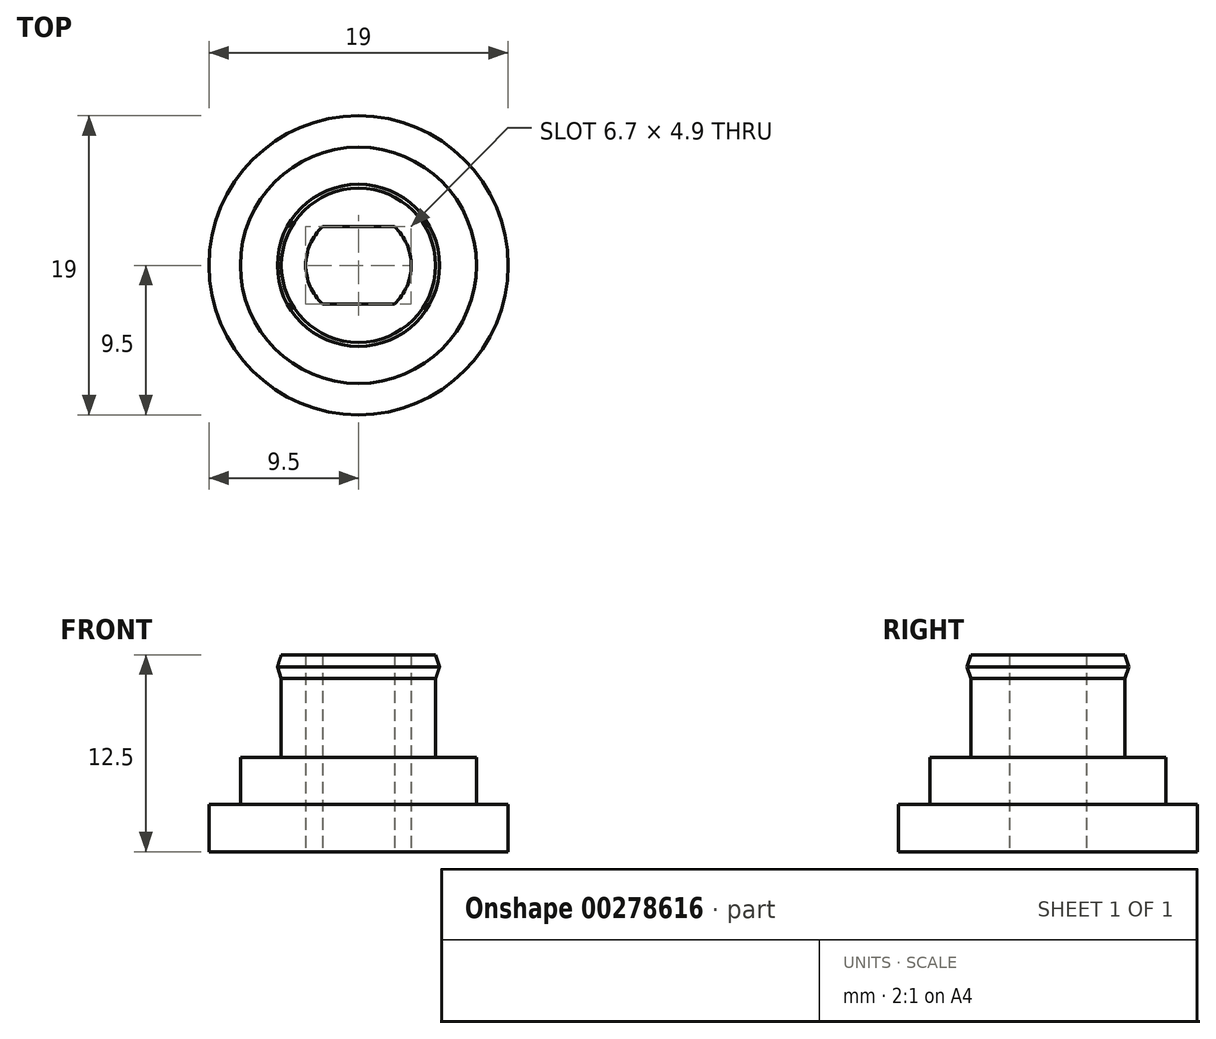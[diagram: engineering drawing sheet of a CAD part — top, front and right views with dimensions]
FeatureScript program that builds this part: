
annotation { "Feature Type Name" : "Feature", "Feature Type Description" : "" }
export const myFeature = defineFeature(function(context is Context, id is Id, definition is map)
    precondition{}
    {
        {
            assignVariable(context, id + "F0", {"name" : "e", "anyValue" : 3});
        }
        {
            assignVariable(context, id + "F1", {"name" : "h1", "anyValue" : 3});
        }
        {
            assignVariable(context, id + "F2", {"name" : "h2", "anyValue" : 6.5});
        }
        {
            var Q0;
            Q0=qCreatedBy(makeId("Top.planeOp"),FACE);
            var sketch = newSketch(context, id + "F3", { "sketchPlane" : qUnion([Q0])});
            skCircle(sketch, "E0", {"center": v(0, 0) * mm, "radius": 9.5 * mm});
            skCircle(sketch, "E1", {"center": v(0, 0) * mm, "radius": 7.5 * mm});
            skCircle(sketch, "E2", {"center": v(0, 0) * mm, "radius": 4.9 * mm});
            skArc(sketch, "E3", {"start": v(-2.28, 2.45) * mm, "mid": v(-3.35, 0) * mm, "end": v(-2.28, -2.45) * mm});
            skLineSegment(sketch, "E4.bottom", {"start": v(2.28, -2.45) * mm, "end": v(-2.28, -2.45) * mm});
            skLineSegment(sketch, "E4.top", {"start": v(2.28, 2.45) * mm, "end": v(-2.28, 2.45) * mm});
            skArc(sketch, "E5.trimOffspring", {"start": v(2.28, -2.45) * mm, "mid": v(3.35, 0) * mm, "end": v(2.28, 2.45) * mm});
            skPoint(sketch, "E6.orphan", {"position": v(3.35, 2.45) * mm});
            skPoint(sketch, "E7.orphan", {"position": v(3.35, -2.45) * mm});
            skPoint(sketch, "E8.orphan", {"position": v(-3.35, -2.45) * mm});
            skPoint(sketch, "E9.orphan", {"position": v(-3.35, 2.45) * mm});
            skSolve(sketch);
        }
        {
            var Q0;
            Q0=makeQuery(id+"F3.imprint","IMPRINT",FACE,{"disambiguationData":[TD([[makeQuery(id+"F3.imprint","IMPRINT",EDGE,{"derivedFrom":sQuery(id+"F3.wireOp",EDGE,"E0")}),1.0]])]});
            var Q1;
            Q1=makeQuery(id+"F3.imprint","IMPRINT",FACE,{"disambiguationData":[TD([[makeQuery(id+"F3.imprint","IMPRINT",EDGE,{"derivedFrom":sQuery(id+"F3.wireOp",EDGE,"E1")}),1.0]])]});
            var Q2;
            Q2=makeQuery(id+"F3.imprint","IMPRINT",FACE,{"disambiguationData":[TD([[makeQuery(id+"F3.imprint","IMPRINT",EDGE,{"derivedFrom":sQuery(id+"F3.wireOp",EDGE,"E2")}),1.0]])]});
            extrude(context, id + "F4", {"entities" : qUnion([Q0, Q1, Q2]), "depth" : (getVariable(context, 'e')) * mm});
        }
        {
            var Q0;
            Q0=makeQuery(id+"F3.imprint","IMPRINT",FACE,{"disambiguationData":[TD([[makeQuery(id+"F3.imprint","IMPRINT",EDGE,{"derivedFrom":sQuery(id+"F3.wireOp",EDGE,"E1")}),1.0]])]});
            var Q1;
            Q1=makeQuery(id+"F3.imprint","IMPRINT",FACE,{"disambiguationData":[TD([[makeQuery(id+"F3.imprint","IMPRINT",EDGE,{"derivedFrom":sQuery(id+"F3.wireOp",EDGE,"E2")}),1.0]])]});
            extrude(context, id + "F5", {"entities" : qUnion([Q0, Q1]), "operationType" : NewBodyOperationType.ADD, "depth" : (getVariable(context, 'e') + getVariable(context, 'h1')) * mm, "offsetDistance" : 25 * mm});
        }
        {
            var Q0;
            Q0=makeQuery(id+"F3.imprint","IMPRINT",FACE,{"disambiguationData":[TD([[makeQuery(id+"F3.imprint","IMPRINT",EDGE,{"derivedFrom":sQuery(id+"F3.wireOp",EDGE,"E2")}),1.0]])]});
            extrude(context, id + "F6", {"entities" : qUnion([Q0]), "operationType" : NewBodyOperationType.ADD, "depth" : (getVariable(context, 'e') + getVariable(context, 'h1') + getVariable(context, 'h2')) * mm});
        }
        {
            var Q0;
            Q0=qCreatedBy(makeId("Front.planeOp"),FACE);
            var sketch = newSketch(context, id + "F7", { "sketchPlane" : qUnion([Q0])});
            skLineSegment(sketch, "E10", {"start": v(0, 0) * mm, "end": v(0, 17.5) * mm, "construction": true});
            skLineSegment(sketch, "E11", {"start": v(-4.9, 6) * mm, "end": v(-4.9, 12.5) * mm});
            skLineSegment(sketch, "E12", {"start": v(4.9, 12.5) * mm, "end": v(4.9, 6) * mm});
            skLineSegment(sketch, "E13.bottom", {"start": v(4.9, 12.5) * mm, "end": v(5.15, 12.5) * mm, "construction": true});
            skLineSegment(sketch, "E13.top", {"start": v(4.9, 11) * mm, "end": v(5.15, 11) * mm, "construction": true});
            skLineSegment(sketch, "E13.left", {"start": v(4.9, 12.5) * mm, "end": v(4.9, 11) * mm, "construction": true});
            skLineSegment(sketch, "E13.right", {"start": v(5.15, 12.5) * mm, "end": v(5.15, 11) * mm, "construction": true});
            skPoint(sketch, "E14", {"position": v(5.15, 11.75) * mm});
            skLineSegment(sketch, "E15", {"start": v(4.9, 12.5) * mm, "end": v(5.15, 11.75) * mm});
            skLineSegment(sketch, "E16", {"start": v(5.15, 11.75) * mm, "end": v(4.9, 11) * mm});
            skLineSegment(sketch, "E17", {"start": v(4.9, 11) * mm, "end": v(4.9, 12.5) * mm});
            skSolve(sketch);
        }
        {
            var Q0;
            Q0=makeQuery(id+"F7.imprint","IMPRINT",FACE,{"disambiguationData":[TD([[makeQuery(id+"F7.imprint","IMPRINT",EDGE,{"derivedFrom":sQuery(id+"F7.wireOp",EDGE,"E15")}),-1.0]])]});
            var Q1;
            Q1=sQuery(id+"F7.wireOp",EDGE,"E10");
            revolve(context, id + "F8", {"operationType" : NewBodyOperationType.ADD, "entities" : qUnion([Q0]), "axis" : qUnion([Q1]), "revolveType" : RevolveType.FULL});
        }
        {
            var Q0;
            Q0=makeQuery(id+"F6.opExtrude","CAP_FACE",FACE,{"disambiguationData":[OSD([sQuery(id+"F3.wireOp",EDGE,"E2"),sQuery(id+"F3.wireOp",EDGE,"E3"),sQuery(id+"F3.wireOp",EDGE,"E4.bottom"),sQuery(id+"F3.wireOp",EDGE,"E4.top"),sQuery(id+"F3.wireOp",EDGE,"E5.trimOffspring")])],"isStart":false});
            cPlane(context, id + "F9", {"entities" : qUnion([Q0]), "cplaneType" : CPlaneType.OFFSET, "offset" : 0 * mm, "width" : 150 * mm, "height" : 150 * mm});
        }
    });
